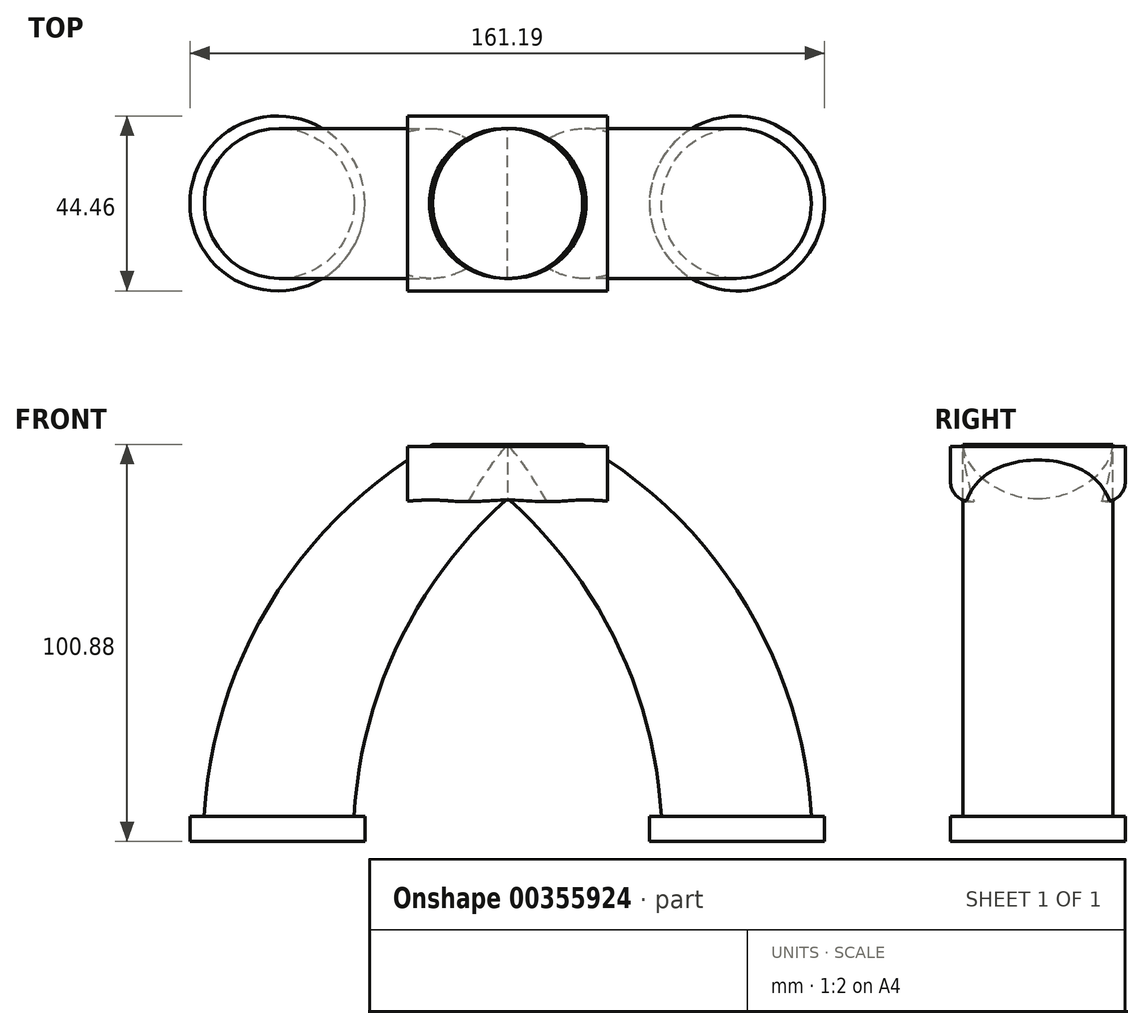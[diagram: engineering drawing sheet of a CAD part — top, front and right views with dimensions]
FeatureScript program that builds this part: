
annotation { "Feature Type Name" : "Feature", "Feature Type Description" : "" }
export const myFeature = defineFeature(function(context is Context, id is Id, definition is map)
    precondition{}
    {
        {
            var Q0;
            Q0=qCreatedBy(makeId("Top.planeOp"),FACE);
            var sketch = newSketch(context, id + "F0", { "sketchPlane" : qUnion([Q0])});
            skLineSegment(sketch, "E0", {"start": v(0, 0) * mm, "end": v(-116.48, 0) * mm, "construction": true});
            skCircle(sketch, "E1", {"center": v(-116.48, 0) * mm, "radius": 19.05 * mm});
            skCircle(sketch, "E2", {"center": v(0, 0) * mm, "radius": 19.05 * mm});
            skLineSegment(sketch, "E3.right", {"start": v(-140, -27.25) * mm, "end": v(-140, 27.25) * mm});
            skPoint(sketch, "E3.middle", {"position": v(-58.24, 0) * mm});
            skPoint(sketch, "E3.left.end.orphan", {"position": v(23.51, 27.25) * mm});
            skPoint(sketch, "E3.left.start.orphan", {"position": v(23.51, -27.25) * mm});
            skSolve(sketch);
        }
        {
            var Q0;
            Q0=qCreatedBy(makeId("Front.planeOp"),FACE);
            var sketch = newSketch(context, id + "F1", { "sketchPlane" : qUnion([Q0])});
            skArc(sketch, "E4", {"start": v(-58.24, 100.88) * mm, "mid": v(-100.88, 58.24) * mm, "end": v(-116.48, 0) * mm});
            skArc(sketch, "E5", {"start": v(0, 0) * mm, "mid": v(-15.6, 58.24) * mm, "end": v(-58.24, 100.88) * mm});
            skSolve(sketch);
        }
        {
            var Q0;
            Q0=makeQuery(id+"F0.imprint","IMPRINT",FACE,{"disambiguationData":[TD([[makeQuery(id+"F0.imprint","IMPRINT",EDGE,{"derivedFrom":sQuery(id+"F0.wireOp",EDGE,"E1")}),1.0]])]});
            var Q1;
            Q1=sQuery(id+"F1.wireOp",EDGE,"E4");
            sweep(context, id + "F2", {"profiles" : qUnion([Q0]), "path" : qUnion([Q1]), "keepProfileOrientation" : true});
        }
        {
            var Q0;
            Q0=makeQuery(id+"F0.imprint","IMPRINT",FACE,{"disambiguationData":[TD([[makeQuery(id+"F0.imprint","IMPRINT",EDGE,{"derivedFrom":sQuery(id+"F0.wireOp",EDGE,"E2")}),1.0]])]});
            var Q1;
            Q1=sQuery(id+"F1.wireOp",EDGE,"E5");
            sweep(context, id + "F3", {"operationType" : NewBodyOperationType.ADD, "profiles" : qUnion([Q0]), "path" : qUnion([Q1]), "keepProfileOrientation" : true});
        }
        {
            var Q0;
            Q0=qCreatedBy(makeId("Top.planeOp"),FACE);
            var sketch = newSketch(context, id + "F4", { "sketchPlane" : qUnion([Q0])});
            skCircle(sketch, "E6", {"center": v(-116.73, 0) * mm, "radius": 22.23 * mm});
            skCircle(sketch, "E7", {"center": v(0, 0) * mm, "radius": 22.23 * mm});
            skSolve(sketch);
        }
        {
            var Q0;
            Q0=makeQuery(id+"F4.imprint","IMPRINT",FACE,{"disambiguationData":[TD([[makeQuery(id+"F4.imprint","IMPRINT",EDGE,{"derivedFrom":sQuery(id+"F4.wireOp",EDGE,"E6")}),1.0]])]});
            var Q1;
            Q1=makeQuery(id+"F4.imprint","IMPRINT",FACE,{"disambiguationData":[TD([[makeQuery(id+"F4.imprint","IMPRINT",EDGE,{"derivedFrom":sQuery(id+"F4.wireOp",EDGE,"E7")}),1.0]])]});
            extrude(context, id + "F5", {"entities" : qUnion([Q0, Q1]), "operationType" : NewBodyOperationType.ADD, "depth" : 6.35 * mm});
        }
        {
            var Q0;
            Q0=makeQuery(id+"F2.opSweep","CAP_FACE",FACE,{"disambiguationData":[OSD([sQuery(id+"F0.wireOp",EDGE,"E1"),sQuery(id+"F1.wireOp",VERTEX,"E4.start")])],"isStart":false});
            var sketch = newSketch(context, id + "F6", { "sketchPlane" : qUnion([Q0])});
            skLineSegment(sketch, "E8.bottom", {"start": v(-32.84, -22.23) * mm, "end": v(-83.64, -22.22) * mm});
            skLineSegment(sketch, "E8.top", {"start": v(-32.84, 22.22) * mm, "end": v(-83.64, 22.23) * mm});
            skLineSegment(sketch, "E8.left", {"start": v(-32.84, -22.23) * mm, "end": v(-32.84, 22.23) * mm});
            skLineSegment(sketch, "E8.right", {"start": v(-83.64, -22.22) * mm, "end": v(-83.64, 22.23) * mm});
            skPoint(sketch, "E8.middle", {"position": v(-58.24, 0) * mm});
            skSolve(sketch);
        }
        {
            var Q0;
            Q0=makeQuery(id+"F6.imprint","IMPRINT",FACE,{"disambiguationData":[TD([[makeQuery(id+"F6.imprint","IMPRINT",EDGE,{"derivedFrom":sQuery(id+"F6.wireOp",EDGE,"E8.bottom")}),-1.0]])]});
            extrude(context, id + "F7", {"entities" : qUnion([Q0]), "operationType" : NewBodyOperationType.ADD, "oppositeDirection" : true, "depth" : 14.48 * mm, "hasSecondDirection" : true, "secondDirectionOppositeDirection" : true, "secondDirectionDepth" : 0.5 * mm, "hasSecondDirectionDraft" : true, "secondDirectionDraftAngle" : 4 * degree, "secondDirectionDraftPullDirection" : true});
        }
        {
            var Q0;
            Q0=makeQuery(id+"F7.opExtrude","CAP_EDGE",EDGE,{"disambiguationData":[OSD([sQuery(id+"F6.wireOp",EDGE,"E8.bottom")])],"isStart":false});
            var Q1;
            Q1=makeQuery(id+"F7.opExtrude","CAP_EDGE",EDGE,{"disambiguationData":[OSD([sQuery(id+"F6.wireOp",EDGE,"E8.top")])],"isStart":false});
            fillet(context, id + "F8", {"entities" : qUnion([Q0, Q1]), "radius" : 5.08 * mm, "tangentPropagation" : true, "allowEdgeOverflow" : false});
        }
    });
